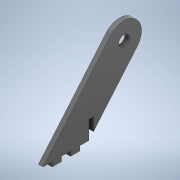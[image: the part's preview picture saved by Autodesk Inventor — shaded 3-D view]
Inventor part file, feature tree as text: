
AUTODESK INVENTOR PART (.ipt)
format: ipt  version: 2020 (Build 240168000, 168)  size: 128,512 bytes
history: native  units: in
note: dims shown in document units (in); Inventor stores cm internally (conversion verified against a paired STEP export)
features: extrude x2, sketch x2
ambient origin geometry x8: Origin, YZ Plane, XZ Plane, XY Plane, X Axis, Y Axis, Z Axis, Center Point
bodies: Solid1 (feature_tree)
feature tree (4):
  extrude  "Extrusion1"  Depth=0.1181in
  extrude  "Extrusion2"  Depth=0.1181in
  sketch  "Sketch1"  dims[d0=1.1811in d1=0.1181in]
  sketch  "Sketch3"  dims[d2=0.2362in d3=0.1181in d4=0.2362in d5=0.1181in d6=0.2362in d7=0.2362in d8=0.2362in d9=1.7717in d10=0.9055in d11=0.1181in d12=0.0in d13=0.2756in d14=0.3937in d15=0.0in d16=0.1181in]
